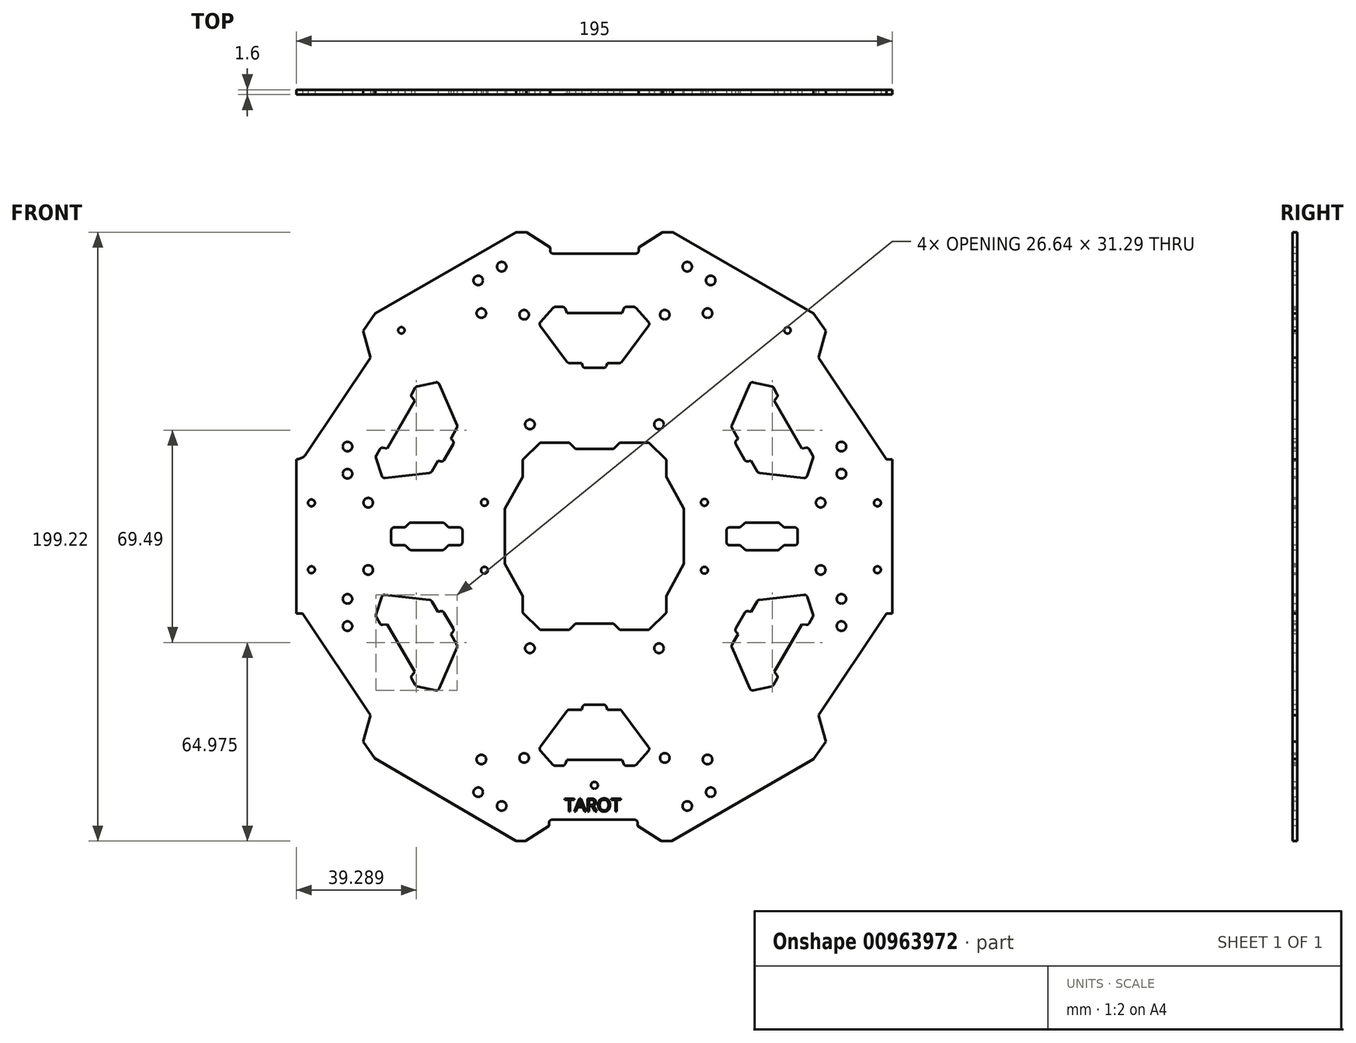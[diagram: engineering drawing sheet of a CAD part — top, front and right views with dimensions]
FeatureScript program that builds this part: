
annotation { "Feature Type Name" : "Feature", "Feature Type Description" : "" }
export const myFeature = defineFeature(function(context is Context, id is Id, definition is map)
    precondition{}
    {
        {
            var Q0;
            Q0=qCreatedBy(makeId("Front.planeOp"),FACE);
            var sketch = newSketch(context, id + "F0", { "sketchPlane" : qUnion([Q0])});
            skLineSegment(sketch, "E0.0", {"start": v(-55.43, 99) * mm, "end": v(57.16, 99) * mm});
            skLineSegment(sketch, "E0.1", {"start": v(57.16, 99) * mm, "end": v(113.45, 1.5) * mm});
            skLineSegment(sketch, "E0.2", {"start": v(113.45, 1.5) * mm, "end": v(55.43, -99) * mm});
            skLineSegment(sketch, "E0.3", {"start": v(55.43, -99) * mm, "end": v(-57.6, -99) * mm});
            skLineSegment(sketch, "E0.4", {"start": v(-57.6, -99) * mm, "end": v(-113.24, -1.13) * mm});
            skLineSegment(sketch, "E0.5", {"start": v(-113.24, -1.13) * mm, "end": v(-55.43, 99) * mm});
            skPoint(sketch, "E0.0.midPoint", {"position": v(0.87, 99) * mm});
            skSolve(sketch);
        }
        {
            var Q0;
            Q0 = qSketchRegion(id + "F0", true);
            extrude(context, id + "F1", {"entities" : qUnion([Q0]), "depth" : 1.6 * mm, "offsetDistance" : 25 * mm});
        }
        {
            var Q0;
            Q0=makeQuery(id+"F1.opExtrude","CAP_FACE",FACE,{"disambiguationData":[OSD([sQuery(id+"F0.wireOp",EDGE,"E0.0"),sQuery(id+"F0.wireOp",EDGE,"E0.1"),sQuery(id+"F0.wireOp",EDGE,"E0.2"),sQuery(id+"F0.wireOp",EDGE,"E0.3"),sQuery(id+"F0.wireOp",EDGE,"E0.4"),sQuery(id+"F0.wireOp",EDGE,"E0.5")])],"isStart":false});
            var sketch = newSketch(context, id + "F2", { "sketchPlane" : qUnion([Q0])});
            skLineSegment(sketch, "E1", {"start": v(0, 0) * mm, "end": v(0, 99) * mm, "construction": true});
            skLineSegment(sketch, "E2", {"start": v(-25.62, 99) * mm, "end": v(-25.62, 82.49) * mm, "construction": true});
            skLineSegment(sketch, "E3", {"start": v(25.63, 99) * mm, "end": v(25.63, 87.55) * mm, "construction": true});
            skLineSegment(sketch, "E4", {"start": v(-25.62, 99) * mm, "end": v(0, 99) * mm, "construction": true});
            skLineSegment(sketch, "E5", {"start": v(25.62, 99) * mm, "end": v(0, 99) * mm, "construction": true});
            skLineSegment(sketch, "E6", {"start": v(-25.62, 99) * mm, "end": v(-33.12, 99) * mm, "construction": true});
            skLineSegment(sketch, "E7", {"start": v(0, 0) * mm, "end": v(-84.33, 48.69) * mm, "construction": true});
            skPoint(sketch, "E7.endSnap0", {"position": v(-84.33, 48.93) * mm});
            skLineSegment(sketch, "E8", {"start": v(-96.83, 27.28) * mm, "end": v(-84.63, 20.24) * mm, "construction": true});
            skLineSegment(sketch, "E9", {"start": v(-71.83, 70.58) * mm, "end": v(-70.08, 69.58) * mm, "construction": true});
            skLineSegment(sketch, "E10", {"start": v(-96.83, 27.28) * mm, "end": v(-84.33, 48.93) * mm, "construction": true});
            skLineSegment(sketch, "E11", {"start": v(-71.83, 70.58) * mm, "end": v(-84.33, 48.93) * mm, "construction": true});
            skLineSegment(sketch, "E12", {"start": v(-70.08, 69.58) * mm, "end": v(-71.83, 70.58) * mm});
            skLineSegment(sketch, "E13", {"start": v(-71.83, 70.58) * mm, "end": v(-55.43, 99) * mm});
            skLineSegment(sketch, "E14", {"start": v(-55.43, 99) * mm, "end": v(-33.12, 99) * mm});
            skLineSegment(sketch, "E15", {"start": v(0, 0) * mm, "end": v(24.48, 42.4) * mm, "construction": true});
            skLineSegment(sketch, "E16", {"start": v(-70.08, 69.58) * mm, "end": v(-34.22, 87.3) * mm});
            skLineSegment(sketch, "E17", {"start": v(-25.62, 99) * mm, "end": v(-31.95, 96) * mm});
            skLineSegment(sketch, "E18", {"start": v(-31.95, 96) * mm, "end": v(-34.22, 87.3) * mm});
            skLineSegment(sketch, "E19.MirrorCS", {"start": v(-95.3, 25.9) * mm, "end": v(-97.04, 26.92) * mm});
            skLineSegment(sketch, "E20.MirrorCS", {"start": v(-97.04, 26.92) * mm, "end": v(-95.3, 25.9) * mm, "construction": true});
            skLineSegment(sketch, "E21.MirrorCS", {"start": v(-99.11, -20.33) * mm, "end": v(-92.7, -14) * mm});
            skLineSegment(sketch, "E22.MirrorCS", {"start": v(-98.55, -27.3) * mm, "end": v(-102.3, -20.81) * mm, "construction": true});
            skLineSegment(sketch, "E23.MirrorCS", {"start": v(-98.55, -27.3) * mm, "end": v(-99.11, -20.33) * mm});
            skPoint(sketch, "E24.MirrorP", {"position": v(-84.54, 48.57) * mm});
            skLineSegment(sketch, "E25.MirrorCS", {"start": v(-98.55, -27.3) * mm, "end": v(-84.25, -19.05) * mm, "construction": true});
            skLineSegment(sketch, "E26.MirrorCS", {"start": v(-97.04, 26.92) * mm, "end": v(-113.45, -1.5) * mm});
            skLineSegment(sketch, "E27.MirrorCS", {"start": v(-95.3, 25.9) * mm, "end": v(-92.7, -14) * mm});
            skLineSegment(sketch, "E28.MirrorCS", {"start": v(-113.45, -1.5) * mm, "end": v(-102.3, -20.81) * mm});
            skLineSegment(sketch, "E29.MirrorCS", {"start": v(70.08, -69.58) * mm, "end": v(71.83, -70.58) * mm});
            skLineSegment(sketch, "E30.MirrorCS", {"start": v(71.83, -70.58) * mm, "end": v(70.08, -69.58) * mm, "construction": true});
            skLineSegment(sketch, "E31.MirrorCS", {"start": v(95.3, -25.9) * mm, "end": v(97.04, -26.92) * mm});
            skLineSegment(sketch, "E32.MirrorCS", {"start": v(97.04, -26.92) * mm, "end": v(95.3, -25.9) * mm, "construction": true});
            skLineSegment(sketch, "E33.MirrorCS", {"start": v(31.95, -96) * mm, "end": v(34.22, -87.3) * mm});
            skLineSegment(sketch, "E34.MirrorCS", {"start": v(98.55, 27.3) * mm, "end": v(99.11, 20.33) * mm});
            skLineSegment(sketch, "E35.MirrorCS", {"start": v(98.55, 27.3) * mm, "end": v(102.3, 20.81) * mm, "construction": true});
            skLineSegment(sketch, "E36.MirrorCS", {"start": v(25.63, -99) * mm, "end": v(33.13, -99) * mm, "construction": true});
            skLineSegment(sketch, "E37.MirrorCS", {"start": v(25.62, -99) * mm, "end": v(31.95, -96) * mm});
            skLineSegment(sketch, "E38.MirrorCS", {"start": v(99.11, 20.33) * mm, "end": v(92.7, 14) * mm});
            skPoint(sketch, "E39.MirrorP", {"position": v(84.33, -48.93) * mm});
            skLineSegment(sketch, "E40.MirrorCS", {"start": v(72.04, -70.22) * mm, "end": v(59.84, -63.17) * mm, "construction": true});
            skLineSegment(sketch, "E41.MirrorCS", {"start": v(95.3, -25.9) * mm, "end": v(92.7, 14) * mm});
            skLineSegment(sketch, "E42.MirrorCS", {"start": v(25.63, -99) * mm, "end": v(25.63, -82.49) * mm, "construction": true});
            skLineSegment(sketch, "E43.MirrorCS", {"start": v(72.04, -70.22) * mm, "end": v(84.54, -48.57) * mm, "construction": true});
            skLineSegment(sketch, "E44.MirrorCS", {"start": v(113.45, 1.5) * mm, "end": v(102.3, 20.81) * mm});
            skLineSegment(sketch, "E45.MirrorCS", {"start": v(97.04, -26.92) * mm, "end": v(113.45, 1.5) * mm});
            skLineSegment(sketch, "E46.MirrorCS", {"start": v(97.04, -26.92) * mm, "end": v(84.54, -48.57) * mm, "construction": true});
            skLineSegment(sketch, "E47.MirrorCS", {"start": v(70.08, -69.58) * mm, "end": v(34.22, -87.3) * mm});
            skPoint(sketch, "E48.MirrorP", {"position": v(84.54, -48.57) * mm});
            skLineSegment(sketch, "E49.MirrorCS", {"start": v(71.83, -70.58) * mm, "end": v(55.43, -99) * mm});
            skLineSegment(sketch, "E50.MirrorCS", {"start": v(55.43, -99) * mm, "end": v(33.12, -99) * mm});
            skLineSegment(sketch, "E51.MirrorCS", {"start": v(98.55, 27.3) * mm, "end": v(84.25, 19.05) * mm, "construction": true});
            skSolve(sketch);
        }
        {
            var Q0;
            Q0=makeQuery(id+"F2.imprint","IMPRINT",FACE,{"disambiguationData":[TD([[makeQuery(id+"F2.imprint","IMPRINT",EDGE,{"derivedFrom":sQuery(id+"F2.wireOp",EDGE,"E12")}),-1.0]])]});
            var Q1;
            {var subQ3=sQuery(id+"F2.wireOp",EDGE,"E19.MirrorCS");Q1=makeQuery(id+"F2.imprint","IMPRINT",FACE,{"disambiguationData":[TD([[makeQuery(id+"F2.imprint","IMPRINT",EDGE,{"derivedFrom":subQ3}),1.0]])]});}
            var Q2;
            Q2=makeQuery(id+"F2.imprint","IMPRINT",FACE,{"disambiguationData":[TD([[makeQuery(id+"F2.imprint","IMPRINT",EDGE,{"derivedFrom":sQuery(id+"F2.wireOp",EDGE,"E29.MirrorCS")}),-1.0]])]});
            var Q3;
            Q3=makeQuery(id+"F2.imprint","IMPRINT",FACE,{"disambiguationData":[TD([[makeQuery(id+"F2.imprint","IMPRINT",EDGE,{"derivedFrom":sQuery(id+"F2.wireOp",EDGE,"E31.MirrorCS")}),1.0]])]});
            extrude(context, id + "F3", {"entities" : qUnion([Q0, Q1, Q2, Q3]), "operationType" : NewBodyOperationType.REMOVE, "oppositeDirection" : true, "depth" : 25 * mm, "offsetDistance" : 25 * mm});
        }
        {
            var Q0;
            Q0=qCreatedBy(makeId("Right.planeOp"),FACE);
            var sketch = newSketch(context, id + "F4", { "sketchPlane" : qUnion([Q0])});
            skLineSegment(sketch, "E52", {"start": v(0, 0) * mm, "end": v(-52.74, 0) * mm});
            skSolve(sketch);
        }
        {
            var Q0;
            Q0=makeQuery(id+"F1.opExtrude","SWEPT_BODY",BODY,{"disambiguationData":[OSD([sQuery(id+"F0.wireOp",EDGE,"E0.0"),sQuery(id+"F0.wireOp",EDGE,"E0.1"),sQuery(id+"F0.wireOp",EDGE,"E0.2"),sQuery(id+"F0.wireOp",EDGE,"E0.3"),sQuery(id+"F0.wireOp",EDGE,"E0.4"),sQuery(id+"F0.wireOp",EDGE,"E0.5")])]});
            var Q1;
            Q1=sQuery(id+"F4.wireOp",EDGE,"E52");
            transform(context, id + "F5", {"entities" : qUnion([Q0]), "transformType" : TransformType.ROTATION, "transformAxis" : qUnion([Q1]), "angle" : 30 * degree, "makeCopy" : false});
        }
        {
            var Q0;
            Q0=makeQuery(id+"F1.opExtrude","CAP_FACE",FACE,{"disambiguationData":[OSD([sQuery(id+"F0.wireOp",EDGE,"E0.0"),sQuery(id+"F0.wireOp",EDGE,"E0.1"),sQuery(id+"F0.wireOp",EDGE,"E0.2"),sQuery(id+"F0.wireOp",EDGE,"E0.3"),sQuery(id+"F0.wireOp",EDGE,"E0.4"),sQuery(id+"F0.wireOp",EDGE,"E0.5")])],"isStart":false});
            var sketch = newSketch(context, id + "F6", { "sketchPlane" : qUnion([Q0])});
            skLineSegment(sketch, "E53", {"start": v(0, 0) * mm, "end": v(0, 92.5) * mm, "construction": true});
            skLineSegment(sketch, "E54", {"start": v(0, 92.5) * mm, "end": v(-14.5, 92.5) * mm});
            skLineSegment(sketch, "E55", {"start": v(0, 92.5) * mm, "end": v(14.5, 92.5) * mm});
            skLineSegment(sketch, "E56", {"start": v(-14.5, 92.5) * mm, "end": v(-14.5, 94.5) * mm});
            skLineSegment(sketch, "E57", {"start": v(-14.5, 94.5) * mm, "end": v(-14.5, 99.5) * mm, "construction": true});
            skLineSegment(sketch, "E58", {"start": v(-14.5, 99.5) * mm, "end": v(-22.25, 99.5) * mm, "construction": true});
            skLineSegment(sketch, "E59", {"start": v(-14.5, 94.5) * mm, "end": v(-22.25, 99.5) * mm});
            skLineSegment(sketch, "E60", {"start": v(-22.25, 99.5) * mm, "end": v(-25.66, 99.5) * mm});
            skLineSegment(sketch, "E61.MirrorCS", {"start": v(14.5, 99.5) * mm, "end": v(22.25, 99.5) * mm, "construction": true});
            skLineSegment(sketch, "E62.MirrorCS", {"start": v(14.5, 94.5) * mm, "end": v(14.5, 99.5) * mm, "construction": true});
            skLineSegment(sketch, "E63.MirrorCS", {"start": v(22.25, 99.5) * mm, "end": v(25.66, 99.5) * mm});
            skLineSegment(sketch, "E64.MirrorCS", {"start": v(14.5, 94.5) * mm, "end": v(22.25, 99.5) * mm});
            skLineSegment(sketch, "E65", {"start": v(14.5, 92.5) * mm, "end": v(14.5, 94.5) * mm});
            skLineSegment(sketch, "E66", {"start": v(-25.66, 99.5) * mm, "end": v(0, 114.32) * mm});
            skLineSegment(sketch, "E67", {"start": v(0, 114.32) * mm, "end": v(25.66, 99.5) * mm});
            skLineSegment(sketch, "E68", {"start": v(-0.38, -92.72) * mm, "end": v(14.12, -92.72) * mm});
            skLineSegment(sketch, "E69", {"start": v(-0.38, -92.72) * mm, "end": v(-14.88, -92.72) * mm});
            skLineSegment(sketch, "E70", {"start": v(14.12, -92.72) * mm, "end": v(14.12, -94.72) * mm});
            skLineSegment(sketch, "E71", {"start": v(14.12, -94.72) * mm, "end": v(14.12, -99.72) * mm, "construction": true});
            skLineSegment(sketch, "E72", {"start": v(14.12, -99.72) * mm, "end": v(21.87, -99.72) * mm, "construction": true});
            skLineSegment(sketch, "E73", {"start": v(14.12, -94.72) * mm, "end": v(21.87, -99.72) * mm});
            skLineSegment(sketch, "E74", {"start": v(21.87, -99.72) * mm, "end": v(25.28, -99.72) * mm});
            skLineSegment(sketch, "E75.MirrorCS", {"start": v(-14.88, -99.72) * mm, "end": v(-22.63, -99.72) * mm, "construction": true});
            skLineSegment(sketch, "E76.MirrorCS", {"start": v(-14.88, -94.72) * mm, "end": v(-14.88, -99.72) * mm, "construction": true});
            skLineSegment(sketch, "E77.MirrorCS", {"start": v(-22.63, -99.72) * mm, "end": v(-26.04, -99.72) * mm});
            skLineSegment(sketch, "E78.MirrorCS", {"start": v(-14.88, -94.72) * mm, "end": v(-22.63, -99.72) * mm});
            skLineSegment(sketch, "E79", {"start": v(-14.88, -92.72) * mm, "end": v(-14.88, -94.72) * mm});
            skLineSegment(sketch, "E80", {"start": v(25.28, -99.72) * mm, "end": v(-0.38, -114.53) * mm});
            skLineSegment(sketch, "E81", {"start": v(-0.38, -114.53) * mm, "end": v(-26.04, -99.72) * mm});
            skSolve(sketch);
        }
        {
            var Q0;
            Q0 = qSketchRegion(id + "F6", true);
            extrude(context, id + "F7", {"entities" : qUnion([Q0]), "operationType" : NewBodyOperationType.REMOVE, "oppositeDirection" : true, "depth" : 25 * mm, "offsetDistance" : 25 * mm});
        }
        {
            var Q0;
            Q0=makeQuery(id+"F1.opExtrude","CAP_FACE",FACE,{"disambiguationData":[OSD([sQuery(id+"F0.wireOp",EDGE,"E0.0"),sQuery(id+"F0.wireOp",EDGE,"E0.1"),sQuery(id+"F0.wireOp",EDGE,"E0.2"),sQuery(id+"F0.wireOp",EDGE,"E0.3"),sQuery(id+"F0.wireOp",EDGE,"E0.4"),sQuery(id+"F0.wireOp",EDGE,"E0.5")])],"isStart":false});
            var sketch = newSketch(context, id + "F8", { "sketchPlane" : qUnion([Q0])});
            skLineSegment(sketch, "E82.bottom", {"start": v(21.13, 36.62) * mm, "end": v(-21.13, 36.62) * mm, "construction": true});
            skLineSegment(sketch, "E82.top", {"start": v(21.12, -36.62) * mm, "end": v(-21.13, -36.62) * mm, "construction": true});
            skLineSegment(sketch, "E82.left", {"start": v(21.13, 36.62) * mm, "end": v(21.12, -36.62) * mm, "construction": true});
            skLineSegment(sketch, "E82.right", {"start": v(-21.13, 36.62) * mm, "end": v(-21.13, -36.62) * mm, "construction": true});
            skPoint(sketch, "E82.middle", {"position": v(0, 0) * mm});
            skCircle(sketch, "E83", {"center": v(-21.13, 36.62) * mm, "radius": 1.57 * mm});
            skCircle(sketch, "E84", {"center": v(21.13, 36.62) * mm, "radius": 1.57 * mm});
            skCircle(sketch, "E85", {"center": v(-21.13, -36.62) * mm, "radius": 1.57 * mm});
            skCircle(sketch, "E86", {"center": v(21.12, -36.62) * mm, "radius": 1.57 * mm});
            skLineSegment(sketch, "E87.bottom", {"start": v(-35.98, 11.1) * mm, "end": v(35.98, 11.1) * mm, "construction": true});
            skLineSegment(sketch, "E87.top", {"start": v(-35.98, -11.1) * mm, "end": v(35.98, -11.1) * mm, "construction": true});
            skLineSegment(sketch, "E87.left", {"start": v(-35.98, 11.1) * mm, "end": v(-35.98, -11.1) * mm, "construction": true});
            skLineSegment(sketch, "E87.right", {"start": v(35.98, 11.1) * mm, "end": v(35.98, -11.1) * mm, "construction": true});
            skCircle(sketch, "E88", {"center": v(-35.98, 11.1) * mm, "radius": 1.13 * mm});
            skCircle(sketch, "E89", {"center": v(-35.98, -11.1) * mm, "radius": 1.13 * mm});
            skCircle(sketch, "E90", {"center": v(35.98, 11.1) * mm, "radius": 1.12 * mm});
            skCircle(sketch, "E91", {"center": v(35.98, -11.1) * mm, "radius": 1.13 * mm});
            skLineSegment(sketch, "E92", {"start": v(-23, 72.5) * mm, "end": v(23, 72.5) * mm, "construction": true});
            skLineSegment(sketch, "E93", {"start": v(0, 72.5) * mm, "end": v(0, 59.38) * mm, "construction": true});
            skCircle(sketch, "E94", {"center": v(-23, 72.5) * mm, "radius": 1.55 * mm});
            skCircle(sketch, "E95", {"center": v(23, 72.5) * mm, "radius": 1.55 * mm});
            skCircle(sketch, "E96.MirrorC", {"center": v(23, -72.5) * mm, "radius": 1.55 * mm});
            skCircle(sketch, "E97.MirrorC", {"center": v(-23, -72.5) * mm, "radius": 1.55 * mm});
            skLineSegment(sketch, "E98.MirrorCS", {"start": v(-23, -72.5) * mm, "end": v(23, -72.5) * mm, "construction": true});
            skLineSegment(sketch, "E99", {"start": v(-37, 73) * mm, "end": v(37, 73) * mm, "construction": true});
            skLineSegment(sketch, "E100", {"start": v(0, 80.25) * mm, "end": v(0, 73) * mm, "construction": true});
            skCircle(sketch, "E101", {"center": v(-37, 73) * mm, "radius": 1.55 * mm});
            skCircle(sketch, "E102", {"center": v(37, 73) * mm, "radius": 1.55 * mm});
            skCircle(sketch, "E103.MirrorC", {"center": v(-37, -73) * mm, "radius": 1.55 * mm});
            skCircle(sketch, "E104.MirrorC", {"center": v(37, -73) * mm, "radius": 1.55 * mm});
            skCircle(sketch, "E105", {"center": v(0, -81.47) * mm, "radius": 1.13 * mm});
            skCircle(sketch, "E106", {"center": v(-63.15, 67.4) * mm, "radius": 1.05 * mm});
            skLineSegment(sketch, "E107", {"start": v(-63.15, 67.4) * mm, "end": v(63.15, 67.4) * mm, "construction": true});
            skLineSegment(sketch, "E108", {"start": v(0, 67.4) * mm, "end": v(0, 57.3) * mm, "construction": true});
            skCircle(sketch, "E109", {"center": v(63.15, 67.4) * mm, "radius": 1.05 * mm});
            skSolve(sketch);
        }
        {
            var Q0;
            Q0=makeQuery(id+"F7.boolean.opBoolean","COPY",EDGE,{"derivedFrom":makeQuery(id+"F7.opExtrude","SWEPT_EDGE",EDGE,{"disambiguationData":[OSD([sQuery(id+"F6.wireOp",EDGE,"E54"),sQuery(id+"F6.wireOp",EDGE,"E56")])]})});
            var Q1;
            Q1=makeQuery(id+"F7.boolean.opBoolean","COPY",EDGE,{"derivedFrom":makeQuery(id+"F7.opExtrude","SWEPT_EDGE",EDGE,{"disambiguationData":[OSD([sQuery(id+"F6.wireOp",EDGE,"E55"),sQuery(id+"F6.wireOp",EDGE,"E65")])]})});
            var Q2;
            Q2=makeQuery(id+"F3.boolean.opBoolean","COPY",EDGE,{"derivedFrom":makeQuery(id+"F3.opExtrude","SWEPT_EDGE",EDGE,{"disambiguationData":[OSD([sQuery(id+"F2.wireOp",EDGE,"3c353f30-4fd9-4b19-be87-6d07171912626.MirrorCS"),sQuery(id+"F2.wireOp",EDGE,"3c353f30-4fd9-4b19-be87-6d07171912627.MirrorCS")])]})});
            var Q3;
            Q3=makeQuery(id+"F3.boolean.opBoolean","COPY",EDGE,{"derivedFrom":makeQuery(id+"F3.opExtrude","SWEPT_EDGE",EDGE,{"disambiguationData":[OSD([sQuery(id+"F2.wireOp",EDGE,"ab6a4181-ef32-43c6-bda4-39222323dd7e2.MirrorCS"),sQuery(id+"F2.wireOp",EDGE,"ab6a4181-ef32-43c6-bda4-39222323dd7e4.MirrorCS")])]})});
            var Q4;
            Q4=makeQuery(id+"F3.boolean.opBoolean","COPY",EDGE,{"derivedFrom":makeQuery(id+"F3.opExtrude","SWEPT_EDGE",EDGE,{"disambiguationData":[OSD([sQuery(id+"F2.wireOp",EDGE,"yAr7u7Sg-ti8k-CcrC-Hcsy-DfrhCiWDHcSb"),sQuery(id+"F2.wireOp",EDGE,"wbw0Cuhm-vE27-KPKq-b3XP-NUPUyRbLNj7i")])]})});
            var Q5;
            Q5=makeQuery(id+"F3.boolean.opBoolean","COPY",EDGE,{"derivedFrom":makeQuery(id+"F3.opExtrude","SWEPT_EDGE",EDGE,{"disambiguationData":[OSD([sQuery(id+"F2.wireOp",EDGE,"5a6e3571-f0e1-4f9f-8eac-d765dfb8e4a70.MirrorCS"),sQuery(id+"F2.wireOp",EDGE,"a7f60a59-f831-41f1-b416-a16ffb49d1590.MirrorCS")])]})});
            var Q6;
            Q6=makeQuery(id+"F7.boolean.opBoolean","COPY",EDGE,{"derivedFrom":makeQuery(id+"F7.opExtrude","SWEPT_EDGE",EDGE,{"disambiguationData":[OSD([sQuery(id+"F6.wireOp",EDGE,"E69"),sQuery(id+"F6.wireOp",EDGE,"E79")])]})});
            var Q7;
            Q7=makeQuery(id+"F7.boolean.opBoolean","COPY",EDGE,{"derivedFrom":makeQuery(id+"F7.opExtrude","SWEPT_EDGE",EDGE,{"disambiguationData":[OSD([sQuery(id+"F6.wireOp",EDGE,"E68"),sQuery(id+"F6.wireOp",EDGE,"E70")])]})});
            fillet(context, id + "F9", {"entities" : qUnion([Q0, Q1, Q2, Q3, Q4, Q5, Q6, Q7]), "radius" : 1 * mm, "tangentPropagation" : true, "allowEdgeOverflow" : false});
        }
        {
            var Q0;
            Q0=makeQuery(id+"F3.boolean.opBoolean","COPY",EDGE,{"derivedFrom":makeQuery(id+"F3.opExtrude","SWEPT_EDGE",EDGE,{"disambiguationData":[OSD([sQuery(id+"F2.wireOp",EDGE,"3c353f30-4fd9-4b19-be87-6d07171912620.MirrorCS"),sQuery(id+"F2.wireOp",EDGE,"3c353f30-4fd9-4b19-be87-6d07171912627.MirrorCS")])]})});
            var Q1;
            Q1=makeQuery(id+"F3.boolean.opBoolean","COPY",EDGE,{"derivedFrom":makeQuery(id+"F3.opExtrude","SWEPT_EDGE",EDGE,{"disambiguationData":[OSD([sQuery(id+"F2.wireOp",EDGE,"ab6a4181-ef32-43c6-bda4-39222323dd7e0.MirrorCS"),sQuery(id+"F2.wireOp",EDGE,"ab6a4181-ef32-43c6-bda4-39222323dd7e4.MirrorCS")])]})});
            var Q2;
            Q2=makeQuery(id+"F3.boolean.opBoolean","COPY",EDGE,{"derivedFrom":makeQuery(id+"F3.opExtrude","SWEPT_EDGE",EDGE,{"disambiguationData":[OSD([sQuery(id+"F2.wireOp",EDGE,"5a6e3571-f0e1-4f9f-8eac-d765dfb8e4a70.MirrorCS"),sQuery(id+"F2.wireOp",EDGE,"EQJ7UQQr-2yyt-cUzk-Uep8-xCyMp42e8Ayk")])]})});
            var Q3;
            Q3=makeQuery(id+"F3.boolean.opBoolean","COPY",EDGE,{"derivedFrom":makeQuery(id+"F3.opExtrude","SWEPT_EDGE",EDGE,{"disambiguationData":[OSD([sQuery(id+"F2.wireOp",EDGE,"wbw0Cuhm-vE27-KPKq-b3XP-NUPUyRbLNj7i"),sQuery(id+"F2.wireOp",EDGE,"E12")])]})});
            fillet(context, id + "F10", {"entities" : qUnion([Q0, Q1, Q2, Q3]), "radius" : 4 * mm, "tangentPropagation" : true, "allowEdgeOverflow" : false});
        }
        {
            var Q0;
            Q0 = qSketchRegion(id + "F8", true);
            extrude(context, id + "F11", {"entities" : qUnion([Q0]), "operationType" : NewBodyOperationType.REMOVE, "oppositeDirection" : true, "depth" : 25 * mm, "offsetDistance" : 25 * mm});
        }
        {
            var Q0;
            Q0=makeQuery(id+"F1.opExtrude","CAP_FACE",FACE,{"disambiguationData":[OSD([sQuery(id+"F0.wireOp",EDGE,"E0.0"),sQuery(id+"F0.wireOp",EDGE,"E0.1"),sQuery(id+"F0.wireOp",EDGE,"E0.2"),sQuery(id+"F0.wireOp",EDGE,"E0.3"),sQuery(id+"F0.wireOp",EDGE,"E0.4"),sQuery(id+"F0.wireOp",EDGE,"E0.5")])],"isStart":false});
            var sketch = newSketch(context, id + "F12", { "sketchPlane" : qUnion([Q0])});
            skCircle(sketch, "E110", {"center": v(-92.57, -10.93) * mm, "radius": 1.13 * mm});
            skLineSegment(sketch, "E111", {"start": v(-92.57, -10.93) * mm, "end": v(-92.57, 10.93) * mm, "construction": true});
            skLineSegment(sketch, "E112", {"start": v(-92.57, 0) * mm, "end": v(0, 0) * mm, "construction": true});
            skCircle(sketch, "E113", {"center": v(-92.57, 10.93) * mm, "radius": 1.13 * mm});
            skLineSegment(sketch, "E114", {"start": v(0, 0) * mm, "end": v(0, 28.32) * mm, "construction": true});
            skCircle(sketch, "E115.MirrorC", {"center": v(92.58, -10.93) * mm, "radius": 1.13 * mm});
            skCircle(sketch, "E116.MirrorC", {"center": v(92.58, 10.93) * mm, "radius": 1.13 * mm});
            skLineSegment(sketch, "E117.MirrorCS", {"start": v(92.58, -10.93) * mm, "end": v(92.58, 10.93) * mm, "construction": true});
            skLineSegment(sketch, "E118.bottom", {"start": v(-74, 11) * mm, "end": v(74, 11) * mm, "construction": true});
            skLineSegment(sketch, "E118.top", {"start": v(-74, -11) * mm, "end": v(74, -11) * mm, "construction": true});
            skLineSegment(sketch, "E118.left", {"start": v(-74, 11) * mm, "end": v(-74, -11) * mm, "construction": true});
            skLineSegment(sketch, "E118.right", {"start": v(74, 11) * mm, "end": v(74, -11) * mm, "construction": true});
            skPoint(sketch, "E118.middle", {"position": v(0, 0) * mm});
            skCircle(sketch, "E119", {"center": v(-74, 11) * mm, "radius": 1.55 * mm});
            skCircle(sketch, "E120", {"center": v(-74, -11) * mm, "radius": 1.55 * mm});
            skCircle(sketch, "E121", {"center": v(74, 11) * mm, "radius": 1.55 * mm});
            skCircle(sketch, "E122", {"center": v(74, -11) * mm, "radius": 1.55 * mm});
            skLineSegment(sketch, "E123", {"start": v(-92.57, -10.92) * mm, "end": v(-80.78, -20.47) * mm, "construction": true});
            skLineSegment(sketch, "E124", {"start": v(-80.78, -20.47) * mm, "end": v(-74, -11) * mm, "construction": true});
            skCircle(sketch, "E125", {"center": v(-80.78, -20.47) * mm, "radius": 1.55 * mm});
            skLineSegment(sketch, "E126", {"start": v(-80.78, -20.47) * mm, "end": v(-80.78, -29.37) * mm, "construction": true});
            skCircle(sketch, "E127", {"center": v(-80.78, -29.37) * mm, "radius": 1.55 * mm});
            skLineSegment(sketch, "E128.MirrorCS", {"start": v(-92.57, 10.92) * mm, "end": v(-80.78, 20.47) * mm, "construction": true});
            skLineSegment(sketch, "E129.MirrorCS", {"start": v(-80.78, 20.47) * mm, "end": v(-74, 11) * mm, "construction": true});
            skCircle(sketch, "E130.MirrorC", {"center": v(-80.78, 20.47) * mm, "radius": 1.55 * mm});
            skCircle(sketch, "E131.MirrorC", {"center": v(-80.78, 29.37) * mm, "radius": 1.55 * mm});
            skLineSegment(sketch, "E132.MirrorCS", {"start": v(-80.78, 20.47) * mm, "end": v(-80.78, 29.37) * mm, "construction": true});
            skCircle(sketch, "E133.MirrorC", {"center": v(80.78, -20.47) * mm, "radius": 1.55 * mm});
            skLineSegment(sketch, "E134.MirrorCS", {"start": v(80.78, -20.47) * mm, "end": v(80.78, -29.37) * mm, "construction": true});
            skCircle(sketch, "E135.MirrorC", {"center": v(80.78, -29.37) * mm, "radius": 1.55 * mm});
            skLineSegment(sketch, "E136.MirrorCS", {"start": v(80.78, 20.47) * mm, "end": v(80.78, 29.37) * mm, "construction": true});
            skCircle(sketch, "E137.MirrorC", {"center": v(80.78, 29.37) * mm, "radius": 1.55 * mm});
            skCircle(sketch, "E138.MirrorC", {"center": v(80.78, 20.47) * mm, "radius": 1.55 * mm});
            skCircle(sketch, "E139", {"center": v(-30.35, -88.21) * mm, "radius": 1.55 * mm});
            skLineSegment(sketch, "E140", {"start": v(-30.35, -88.21) * mm, "end": v(-38.03, -83.71) * mm, "construction": true});
            skCircle(sketch, "E141", {"center": v(-38.03, -83.71) * mm, "radius": 1.55 * mm});
            skLineSegment(sketch, "E142", {"start": v(-30.35, -88.21) * mm, "end": v(30.35, -88.21) * mm, "construction": true});
            skLineSegment(sketch, "E143", {"start": v(0, -88.21) * mm, "end": v(0, -43.95) * mm, "construction": true});
            skCircle(sketch, "E144.MirrorC", {"center": v(38.03, -83.71) * mm, "radius": 1.55 * mm});
            skCircle(sketch, "E145.MirrorC", {"center": v(30.35, -88.21) * mm, "radius": 1.55 * mm});
            skLineSegment(sketch, "E146.MirrorCS", {"start": v(30.35, -88.21) * mm, "end": v(38.03, -83.71) * mm, "construction": true});
            skCircle(sketch, "E147.MirrorC", {"center": v(-30.35, 88.21) * mm, "radius": 1.55 * mm});
            skLineSegment(sketch, "E148.MirrorCS", {"start": v(-30.35, 88.21) * mm, "end": v(-38.03, 83.71) * mm, "construction": true});
            skCircle(sketch, "E149.MirrorC", {"center": v(30.35, 88.21) * mm, "radius": 1.55 * mm});
            skCircle(sketch, "E150.MirrorC", {"center": v(-38.03, 83.71) * mm, "radius": 1.55 * mm});
            skCircle(sketch, "E151.MirrorC", {"center": v(38.03, 83.71) * mm, "radius": 1.55 * mm});
            skLineSegment(sketch, "E152.MirrorCS", {"start": v(30.35, 88.21) * mm, "end": v(38.03, 83.71) * mm, "construction": true});
            skLineSegment(sketch, "E153.MirrorCS", {"start": v(0, 88.21) * mm, "end": v(0, 43.95) * mm, "construction": true});
            skLineSegment(sketch, "E154.MirrorCS", {"start": v(-30.35, 88.21) * mm, "end": v(30.35, 88.21) * mm, "construction": true});
            skSolve(sketch);
        }
        {
            var Q0;
            Q0 = qSketchRegion(id + "F12", true);
            extrude(context, id + "F13", {"entities" : qUnion([Q0]), "operationType" : NewBodyOperationType.REMOVE, "oppositeDirection" : true, "depth" : 25 * mm, "offsetDistance" : 25 * mm});
        }
        {
            var Q0;
            Q0=makeQuery(id+"F1.opExtrude","CAP_FACE",FACE,{"disambiguationData":[OSD([sQuery(id+"F0.wireOp",EDGE,"E0.0"),sQuery(id+"F0.wireOp",EDGE,"E0.1"),sQuery(id+"F0.wireOp",EDGE,"E0.2"),sQuery(id+"F0.wireOp",EDGE,"E0.3"),sQuery(id+"F0.wireOp",EDGE,"E0.4"),sQuery(id+"F0.wireOp",EDGE,"E0.5")])],"isStart":false});
            var sketch = newSketch(context, id + "F14", { "sketchPlane" : qUnion([Q0])});
            skText(sketch, "E155", { "text": "TAROT", "fontName": "OpenSans-Regular.ttf"});
            const initialGuessF14  = {"E155": [-0.0098, -0.09001, 1, 0, 0.00425]};
            skSetInitialGuess(sketch, initialGuessF14);
            skSolve(sketch);
        }
        {
            var Q0;
            Q0 = qSketchRegion(id + "F14", true);
            extrude(context, id + "F15", {"entities" : qUnion([Q0]), "operationType" : NewBodyOperationType.REMOVE, "oppositeDirection" : true, "depth" : .3 * mm, "offsetDistance" : 25 * mm});
        }
        {
            var Q0;
            {var subQ0=sQuery(id+"F0.wireOp",EDGE,"E0.5");var subQ1=sQuery(id+"F0.wireOp",EDGE,"E0.4");var subQ2=sQuery(id+"F0.wireOp",EDGE,"E0.3");var subQ3=sQuery(id+"F0.wireOp",EDGE,"E0.2");var subQ4=sQuery(id+"F0.wireOp",EDGE,"E0.1");var subQ5=sQuery(id+"F0.wireOp",EDGE,"E0.0");Q0=makeQuery(id+"F15.boolean.opBoolean","SPLIT",FACE,{"disambiguationData":[TD([makeQuery(id+"F1.opExtrude","SWEPT_FACE",FACE,{"disambiguationData":[OSD([subQ5])]})])],"derivedFrom":makeQuery(id+"F1.opExtrude","CAP_FACE",FACE,{"disambiguationData":[OSD([subQ5,subQ4,subQ3,subQ2,subQ1,subQ0])],"isStart":false})});}
            var sketch = newSketch(context, id + "F16", { "sketchPlane" : qUnion([Q0])});
            skLineSegment(sketch, "E156.left", {"start": v(-29.25, 9) * mm, "end": v(-29.25, 0) * mm});
            skPoint(sketch, "E156.middle", {"position": v(0, 0) * mm});
            skLineSegment(sketch, "E157.bottom", {"start": v(-6.25, 28.6) * mm, "end": v(0, 28.6) * mm});
            skLineSegment(sketch, "E158", {"start": v(-29.25, 9) * mm, "end": v(-23.46, 19.5) * mm});
            skLineSegment(sketch, "E159", {"start": v(-23.46, 19.5) * mm, "end": v(-23.46, 25) * mm});
            skLineSegment(sketch, "E160", {"start": v(-23.46, 25) * mm, "end": v(-17.75, 30.6) * mm});
            skLineSegment(sketch, "E161", {"start": v(-17.75, 30.6) * mm, "end": v(-8.25, 30.6) * mm});
            skLineSegment(sketch, "E162", {"start": v(-8.25, 30.6) * mm, "end": v(-6.25, 28.6) * mm});
            skLineSegment(sketch, "E163", {"start": v(-29.25, 0) * mm, "end": v(0, 0) * mm, "construction": true});
            skLineSegment(sketch, "E164", {"start": v(0, 28.6) * mm, "end": v(0, 0) * mm, "construction": true});
            skPoint(sketch, "E165.orphan", {"position": v(6.25, 28.6) * mm});
            skPoint(sketch, "E166.orphan", {"position": v(-29.25, -9) * mm});
            skLineSegment(sketch, "E167.MirrorCS", {"start": v(8.25, 30.6) * mm, "end": v(6.25, 28.6) * mm});
            skLineSegment(sketch, "E168.MirrorCS", {"start": v(23.46, 19.5) * mm, "end": v(23.46, 25) * mm});
            skLineSegment(sketch, "E169.MirrorCS", {"start": v(23.46, 25) * mm, "end": v(17.75, 30.6) * mm});
            skLineSegment(sketch, "E170.MirrorCS", {"start": v(29.25, 9) * mm, "end": v(29.25, 0) * mm});
            skLineSegment(sketch, "E171.MirrorCS", {"start": v(17.75, 30.6) * mm, "end": v(8.25, 30.6) * mm});
            skLineSegment(sketch, "E172.MirrorCS", {"start": v(29.25, 9) * mm, "end": v(23.46, 19.5) * mm});
            skLineSegment(sketch, "E173", {"start": v(0, 28.6) * mm, "end": v(6.25, 28.6) * mm});
            skLineSegment(sketch, "E174.MirrorCS", {"start": v(-8.25, -30.6) * mm, "end": v(-6.25, -28.6) * mm});
            skLineSegment(sketch, "E175.MirrorCS", {"start": v(8.25, -30.6) * mm, "end": v(6.25, -28.6) * mm});
            skLineSegment(sketch, "E176.MirrorCS", {"start": v(-29.25, -9) * mm, "end": v(-23.46, -19.5) * mm});
            skLineSegment(sketch, "E177.MirrorCS", {"start": v(-29.25, -9) * mm, "end": v(-29.25, 0) * mm});
            skPoint(sketch, "E178.MirrorP", {"position": v(6.25, -28.6) * mm});
            skLineSegment(sketch, "E179.MirrorCS", {"start": v(23.46, -19.5) * mm, "end": v(23.46, -25) * mm});
            skLineSegment(sketch, "E180.MirrorCS", {"start": v(29.25, -9) * mm, "end": v(23.46, -19.5) * mm});
            skPoint(sketch, "E181.MirrorP", {"position": v(-29.25, 9) * mm});
            skLineSegment(sketch, "E182.MirrorCS", {"start": v(-23.46, -19.5) * mm, "end": v(-23.46, -25) * mm});
            skLineSegment(sketch, "E183.MirrorCS", {"start": v(-6.25, -28.6) * mm, "end": v(0, -28.6) * mm});
            skLineSegment(sketch, "E184.MirrorCS", {"start": v(17.75, -30.6) * mm, "end": v(8.25, -30.6) * mm});
            skLineSegment(sketch, "E185.MirrorCS", {"start": v(-17.75, -30.6) * mm, "end": v(-8.25, -30.6) * mm});
            skLineSegment(sketch, "E186.MirrorCS", {"start": v(29.25, -9) * mm, "end": v(29.25, 0) * mm});
            skLineSegment(sketch, "E187.MirrorCS", {"start": v(23.46, -25) * mm, "end": v(17.75, -30.6) * mm});
            skLineSegment(sketch, "E188.MirrorCS", {"start": v(0, -28.6) * mm, "end": v(6.25, -28.6) * mm});
            skLineSegment(sketch, "E189.MirrorCS", {"start": v(0, -28.6) * mm, "end": v(0, 0) * mm, "construction": true});
            skLineSegment(sketch, "E190.MirrorCS", {"start": v(-23.46, -25) * mm, "end": v(-17.75, -30.6) * mm});
            skLineSegment(sketch, "E191", {"start": v(0, 0) * mm, "end": v(0, 73.1) * mm, "construction": true});
            skLineSegment(sketch, "E192", {"start": v(0, 73.1) * mm, "end": v(9, 73.1) * mm});
            skLineSegment(sketch, "E193", {"start": v(9, 73.1) * mm, "end": v(9.5, 74.4) * mm});
            skLineSegment(sketch, "E194", {"start": v(10.44, 75.05) * mm, "end": v(12.8, 75.05) * mm});
            skLineSegment(sketch, "E195", {"start": v(2.98, 55.1) * mm, "end": v(0, 55.1) * mm});
            skLineSegment(sketch, "E196", {"start": v(3.94, 55.85) * mm, "end": v(4.17, 56.7) * mm});
            skLineSegment(sketch, "E197", {"start": v(4.17, 56.7) * mm, "end": v(8.16, 56.7) * mm});
            skLineSegment(sketch, "E198", {"start": v(13.55, 74.72) * mm, "end": v(17.65, 70.16) * mm});
            skLineSegment(sketch, "E199", {"start": v(17.71, 68.9) * mm, "end": v(8.97, 57.1) * mm});
            skPoint(sketch, "E200.visualSharp", {"position": v(3.75, 55.1) * mm});
            skArc(sketch, "E200.filletArc", {"start": v(2.98, 55.1) * mm, "mid": v(3.59, 55.3) * mm, "end": v(3.94, 55.85) * mm});
            skPoint(sketch, "E201.visualSharp", {"position": v(8.67, 56.7) * mm});
            skArc(sketch, "E201.filletArc", {"start": v(8.16, 56.7) * mm, "mid": v(8.61, 56.8) * mm, "end": v(8.97, 57.1) * mm});
            skPoint(sketch, "E202.visualSharp", {"position": v(18.2, 69.55) * mm});
            skArc(sketch, "E202.filletArc", {"start": v(17.71, 68.9) * mm, "mid": v(17.9, 69.54) * mm, "end": v(17.65, 70.16) * mm});
            skPoint(sketch, "E203.visualSharp", {"position": v(13.25, 75.05) * mm});
            skArc(sketch, "E203.filletArc", {"start": v(13.55, 74.72) * mm, "mid": v(13.21, 74.96) * mm, "end": v(12.8, 75.05) * mm});
            skPoint(sketch, "E204.visualSharp", {"position": v(9.75, 75.05) * mm});
            skArc(sketch, "E204.filletArc", {"start": v(10.44, 75.05) * mm, "mid": v(9.87, 74.87) * mm, "end": v(9.5, 74.4) * mm});
            skArc(sketch, "E205.MirrorCS", {"start": v(-13.55, 74.72) * mm, "mid": v(-13.21, 74.96) * mm, "end": v(-12.8, 75.05) * mm});
            skArc(sketch, "E206.MirrorCS", {"start": v(-2.98, 55.1) * mm, "mid": v(-3.59, 55.3) * mm, "end": v(-3.94, 55.85) * mm});
            skArc(sketch, "E207.MirrorCS", {"start": v(-17.71, 68.9) * mm, "mid": v(-17.9, 69.54) * mm, "end": v(-17.65, 70.16) * mm});
            skLineSegment(sketch, "E208.MirrorCS", {"start": v(-10.44, 75.05) * mm, "end": v(-12.8, 75.05) * mm});
            skArc(sketch, "E209.MirrorCS", {"start": v(-10.44, 75.05) * mm, "mid": v(-9.87, 74.87) * mm, "end": v(-9.5, 74.4) * mm});
            skArc(sketch, "E210.MirrorCS", {"start": v(-8.16, 56.7) * mm, "mid": v(-8.61, 56.8) * mm, "end": v(-8.97, 57.1) * mm});
            skLineSegment(sketch, "E211.MirrorCS", {"start": v(-3.94, 55.85) * mm, "end": v(-4.17, 56.7) * mm});
            skLineSegment(sketch, "E212.MirrorCS", {"start": v(-9, 73.1) * mm, "end": v(-9.5, 74.4) * mm});
            skLineSegment(sketch, "E213.MirrorCS", {"start": v(-4.17, 56.7) * mm, "end": v(-8.16, 56.7) * mm});
            skLineSegment(sketch, "E214.MirrorCS", {"start": v(-2.98, 55.1) * mm, "end": v(0, 55.1) * mm});
            skLineSegment(sketch, "E215.MirrorCS", {"start": v(-13.55, 74.72) * mm, "end": v(-17.65, 70.16) * mm});
            skPoint(sketch, "E216.MirrorP", {"position": v(-18.2, 69.55) * mm});
            skLineSegment(sketch, "E217.MirrorCS", {"start": v(0, 73.1) * mm, "end": v(-9, 73.1) * mm});
            skPoint(sketch, "E218.MirrorP", {"position": v(-3.75, 55.1) * mm});
            skPoint(sketch, "E219.MirrorP", {"position": v(-9.75, 75.05) * mm});
            skPoint(sketch, "E220.MirrorP", {"position": v(-13.25, 75.05) * mm});
            skPoint(sketch, "E221.MirrorP", {"position": v(-8.67, 56.7) * mm});
            skLineSegment(sketch, "E222.MirrorCS", {"start": v(-17.71, 68.9) * mm, "end": v(-8.97, 57.1) * mm});
            skPoint(sketch, "E223.1.0", {"position": v(-53.44, 20.84) * mm});
            skPoint(sketch, "E223.1.1", {"position": v(-60.12, 45.97) * mm});
            skPoint(sketch, "E223.1.2", {"position": v(-71.62, 26.05) * mm});
            skPoint(sketch, "E223.1.3", {"position": v(-49.6, 24.3) * mm});
            skLineSegment(sketch, "E223.1.4", {"start": v(-68.52, 19.1) * mm, "end": v(-53.94, 20.79) * mm});
            skPoint(sketch, "E223.1.5", {"position": v(-51.13, 50.54) * mm});
            skLineSegment(sketch, "E223.1.6", {"start": v(-63.3, 36.55) * mm, "end": v(-67.8, 28.76) * mm});
            skPoint(sketch, "E223.1.7", {"position": v(-69.87, 29.08) * mm});
            skPoint(sketch, "E223.1.8", {"position": v(-58.37, 49) * mm});
            skLineSegment(sketch, "E223.1.9", {"start": v(-50.8, 49.79) * mm, "end": v(-44.97, 36.32) * mm});
            skLineSegment(sketch, "E223.1.10", {"start": v(-71.48, 25.62) * mm, "end": v(-69.59, 19.8) * mm});
            skLineSegment(sketch, "E223.1.11", {"start": v(-57.93, 49.1) * mm, "end": v(-51.93, 50.37) * mm});
            skLineSegment(sketch, "E223.1.12", {"start": v(-63.3, 36.55) * mm, "end": v(-58.8, 44.34) * mm});
            skPoint(sketch, "E223.1.13", {"position": v(-45.84, 30.8) * mm});
            skPoint(sketch, "E223.1.14", {"position": v(-69.33, 19.01) * mm});
            skPoint(sketch, "E223.1.15", {"position": v(-44.77, 35.86) * mm});
            skLineSegment(sketch, "E223.1.16", {"start": v(-46.23, 30.13) * mm, "end": v(-47.72, 27.55) * mm});
            skLineSegment(sketch, "E223.1.17", {"start": v(-49.2, 24.97) * mm, "end": v(-47.72, 27.55) * mm});
            skLineSegment(sketch, "E223.1.18", {"start": v(-58.8, 44.34) * mm, "end": v(-59.69, 45.44) * mm});
            skArc(sketch, "E223.1.19", {"start": v(-70.21, 28.49) * mm, "mid": v(-69.78, 28.89) * mm, "end": v(-69.2, 28.97) * mm});
            skArc(sketch, "E223.1.20", {"start": v(-49.2, 24.97) * mm, "mid": v(-49.7, 24.55) * mm, "end": v(-50.34, 24.5) * mm});
            skArc(sketch, "E223.1.21", {"start": v(-45.02, 35.42) * mm, "mid": v(-44.89, 35.86) * mm, "end": v(-44.97, 36.32) * mm});
            skLineSegment(sketch, "E223.1.22", {"start": v(-46.4, 31.34) * mm, "end": v(-47.02, 31.96) * mm});
            skLineSegment(sketch, "E223.1.23", {"start": v(-51.19, 24.74) * mm, "end": v(-53.19, 21.28) * mm});
            skLineSegment(sketch, "E223.1.24", {"start": v(-70.21, 28.49) * mm, "end": v(-71.4, 26.43) * mm});
            skArc(sketch, "E223.1.25", {"start": v(-46.23, 30.13) * mm, "mid": v(-46.1, 30.76) * mm, "end": v(-46.4, 31.34) * mm});
            skArc(sketch, "E223.1.26", {"start": v(-68.52, 19.1) * mm, "mid": v(-69.17, 19.26) * mm, "end": v(-69.59, 19.8) * mm});
            skArc(sketch, "E223.1.27", {"start": v(-50.8, 49.79) * mm, "mid": v(-51.27, 50.28) * mm, "end": v(-51.93, 50.37) * mm});
            skArc(sketch, "E223.1.28", {"start": v(-71.48, 25.62) * mm, "mid": v(-71.53, 26.04) * mm, "end": v(-71.4, 26.43) * mm});
            skLineSegment(sketch, "E223.1.29", {"start": v(-47.02, 31.96) * mm, "end": v(-45.02, 35.42) * mm});
            skLineSegment(sketch, "E223.1.30", {"start": v(-59.78, 46.56) * mm, "end": v(-58.6, 48.62) * mm});
            skArc(sketch, "E223.1.31", {"start": v(-53.19, 21.28) * mm, "mid": v(-53.5, 20.94) * mm, "end": v(-53.94, 20.79) * mm});
            skLineSegment(sketch, "E223.1.32", {"start": v(-67.8, 28.76) * mm, "end": v(-69.2, 28.97) * mm});
            skLineSegment(sketch, "E223.1.33", {"start": v(-50.34, 24.5) * mm, "end": v(-51.19, 24.74) * mm});
            skArc(sketch, "E223.1.34", {"start": v(-59.78, 46.56) * mm, "mid": v(-59.9, 45.99) * mm, "end": v(-59.69, 45.44) * mm});
            skArc(sketch, "E223.1.35", {"start": v(-57.93, 49.1) * mm, "mid": v(-58.31, 48.93) * mm, "end": v(-58.6, 48.62) * mm});
            skPoint(sketch, "E223.2.0", {"position": v(-44.77, -35.86) * mm});
            skPoint(sketch, "E223.2.1", {"position": v(-69.87, -29.08) * mm});
            skPoint(sketch, "E223.2.2", {"position": v(-58.37, -49) * mm});
            skPoint(sketch, "E223.2.3", {"position": v(-45.84, -30.8) * mm});
            skLineSegment(sketch, "E223.2.4", {"start": v(-50.8, -49.79) * mm, "end": v(-44.97, -36.32) * mm});
            skPoint(sketch, "E223.2.5", {"position": v(-69.33, -19.01) * mm});
            skLineSegment(sketch, "E223.2.6", {"start": v(-63.3, -36.55) * mm, "end": v(-58.8, -44.34) * mm});
            skPoint(sketch, "E223.2.7", {"position": v(-60.12, -45.97) * mm});
            skPoint(sketch, "E223.2.8", {"position": v(-71.62, -26.05) * mm});
            skLineSegment(sketch, "E223.2.9", {"start": v(-68.52, -19.1) * mm, "end": v(-53.94, -20.79) * mm});
            skLineSegment(sketch, "E223.2.10", {"start": v(-57.93, -49.1) * mm, "end": v(-51.93, -50.37) * mm});
            skLineSegment(sketch, "E223.2.11", {"start": v(-71.48, -25.62) * mm, "end": v(-69.59, -19.8) * mm});
            skLineSegment(sketch, "E223.2.12", {"start": v(-63.3, -36.55) * mm, "end": v(-67.8, -28.76) * mm});
            skPoint(sketch, "E223.2.13", {"position": v(-49.6, -24.3) * mm});
            skPoint(sketch, "E223.2.14", {"position": v(-51.13, -50.54) * mm});
            skPoint(sketch, "E223.2.15", {"position": v(-53.44, -20.84) * mm});
            skLineSegment(sketch, "E223.2.16", {"start": v(-49.2, -24.97) * mm, "end": v(-47.72, -27.55) * mm});
            skLineSegment(sketch, "E223.2.17", {"start": v(-46.23, -30.13) * mm, "end": v(-47.72, -27.55) * mm});
            skLineSegment(sketch, "E223.2.18", {"start": v(-67.8, -28.76) * mm, "end": v(-69.2, -28.97) * mm});
            skArc(sketch, "E223.2.19", {"start": v(-59.78, -46.56) * mm, "mid": v(-59.9, -45.99) * mm, "end": v(-59.69, -45.44) * mm});
            skArc(sketch, "E223.2.20", {"start": v(-46.23, -30.13) * mm, "mid": v(-46.1, -30.76) * mm, "end": v(-46.4, -31.34) * mm});
            skArc(sketch, "E223.2.21", {"start": v(-53.19, -21.28) * mm, "mid": v(-53.5, -20.94) * mm, "end": v(-53.94, -20.79) * mm});
            skLineSegment(sketch, "E223.2.22", {"start": v(-50.34, -24.5) * mm, "end": v(-51.19, -24.74) * mm});
            skLineSegment(sketch, "E223.2.23", {"start": v(-47.02, -31.96) * mm, "end": v(-45.02, -35.42) * mm});
            skLineSegment(sketch, "E223.2.24", {"start": v(-59.78, -46.56) * mm, "end": v(-58.6, -48.62) * mm});
            skArc(sketch, "E223.2.25", {"start": v(-49.2, -24.97) * mm, "mid": v(-49.7, -24.55) * mm, "end": v(-50.34, -24.5) * mm});
            skArc(sketch, "E223.2.26", {"start": v(-50.8, -49.79) * mm, "mid": v(-51.27, -50.28) * mm, "end": v(-51.93, -50.37) * mm});
            skArc(sketch, "E223.2.27", {"start": v(-68.52, -19.1) * mm, "mid": v(-69.17, -19.26) * mm, "end": v(-69.59, -19.8) * mm});
            skArc(sketch, "E223.2.28", {"start": v(-57.93, -49.1) * mm, "mid": v(-58.31, -48.93) * mm, "end": v(-58.6, -48.62) * mm});
            skLineSegment(sketch, "E223.2.29", {"start": v(-51.19, -24.74) * mm, "end": v(-53.19, -21.28) * mm});
            skLineSegment(sketch, "E223.2.30", {"start": v(-70.21, -28.49) * mm, "end": v(-71.4, -26.43) * mm});
            skArc(sketch, "E223.2.31", {"start": v(-45.02, -35.42) * mm, "mid": v(-44.89, -35.86) * mm, "end": v(-44.97, -36.32) * mm});
            skLineSegment(sketch, "E223.2.32", {"start": v(-58.8, -44.34) * mm, "end": v(-59.69, -45.44) * mm});
            skLineSegment(sketch, "E223.2.33", {"start": v(-46.4, -31.34) * mm, "end": v(-47.02, -31.96) * mm});
            skArc(sketch, "E223.2.34", {"start": v(-70.21, -28.49) * mm, "mid": v(-69.78, -28.89) * mm, "end": v(-69.2, -28.97) * mm});
            skArc(sketch, "E223.2.35", {"start": v(-71.48, -25.62) * mm, "mid": v(-71.53, -26.04) * mm, "end": v(-71.4, -26.43) * mm});
            skPoint(sketch, "E223.3.0", {"position": v(8.67, -56.7) * mm});
            skPoint(sketch, "E223.3.1", {"position": v(-9.75, -75.05) * mm});
            skPoint(sketch, "E223.3.2", {"position": v(13.25, -75.05) * mm});
            skPoint(sketch, "E223.3.3", {"position": v(3.75, -55.1) * mm});
            skLineSegment(sketch, "E223.3.4", {"start": v(17.71, -68.9) * mm, "end": v(8.97, -57.1) * mm});
            skPoint(sketch, "E223.3.5", {"position": v(-18.2, -69.55) * mm});
            skLineSegment(sketch, "E223.3.6", {"start": v(0, -73.1) * mm, "end": v(9, -73.1) * mm});
            skPoint(sketch, "E223.3.7", {"position": v(9.75, -75.05) * mm});
            skPoint(sketch, "E223.3.8", {"position": v(-13.25, -75.05) * mm});
            skLineSegment(sketch, "E223.3.9", {"start": v(-17.71, -68.9) * mm, "end": v(-8.97, -57.1) * mm});
            skLineSegment(sketch, "E223.3.10", {"start": v(13.55, -74.72) * mm, "end": v(17.65, -70.16) * mm});
            skLineSegment(sketch, "E223.3.11", {"start": v(-13.55, -74.72) * mm, "end": v(-17.65, -70.16) * mm});
            skLineSegment(sketch, "E223.3.12", {"start": v(0, -73.1) * mm, "end": v(-9, -73.1) * mm});
            skPoint(sketch, "E223.3.13", {"position": v(-3.75, -55.1) * mm});
            skPoint(sketch, "E223.3.14", {"position": v(18.2, -69.55) * mm});
            skPoint(sketch, "E223.3.15", {"position": v(-8.67, -56.7) * mm});
            skLineSegment(sketch, "E223.3.16", {"start": v(-2.98, -55.1) * mm, "end": v(0, -55.1) * mm});
            skLineSegment(sketch, "E223.3.17", {"start": v(2.98, -55.1) * mm, "end": v(0, -55.1) * mm});
            skLineSegment(sketch, "E223.3.18", {"start": v(-9, -73.1) * mm, "end": v(-9.5, -74.4) * mm});
            skArc(sketch, "E223.3.19", {"start": v(10.44, -75.05) * mm, "mid": v(9.87, -74.87) * mm, "end": v(9.5, -74.4) * mm});
            skArc(sketch, "E223.3.20", {"start": v(2.98, -55.1) * mm, "mid": v(3.59, -55.3) * mm, "end": v(3.94, -55.85) * mm});
            skArc(sketch, "E223.3.21", {"start": v(-8.16, -56.7) * mm, "mid": v(-8.61, -56.8) * mm, "end": v(-8.97, -57.1) * mm});
            skLineSegment(sketch, "E223.3.22", {"start": v(-3.94, -55.85) * mm, "end": v(-4.17, -56.7) * mm});
            skLineSegment(sketch, "E223.3.23", {"start": v(4.17, -56.7) * mm, "end": v(8.16, -56.7) * mm});
            skLineSegment(sketch, "E223.3.24", {"start": v(10.44, -75.05) * mm, "end": v(12.8, -75.05) * mm});
            skArc(sketch, "E223.3.25", {"start": v(-2.98, -55.1) * mm, "mid": v(-3.59, -55.3) * mm, "end": v(-3.94, -55.85) * mm});
            skArc(sketch, "E223.3.26", {"start": v(17.71, -68.9) * mm, "mid": v(17.9, -69.54) * mm, "end": v(17.65, -70.16) * mm});
            skArc(sketch, "E223.3.27", {"start": v(-17.71, -68.9) * mm, "mid": v(-17.9, -69.54) * mm, "end": v(-17.65, -70.16) * mm});
            skArc(sketch, "E223.3.28", {"start": v(13.55, -74.72) * mm, "mid": v(13.21, -74.96) * mm, "end": v(12.8, -75.05) * mm});
            skLineSegment(sketch, "E223.3.29", {"start": v(-4.17, -56.7) * mm, "end": v(-8.16, -56.7) * mm});
            skLineSegment(sketch, "E223.3.30", {"start": v(-10.44, -75.05) * mm, "end": v(-12.8, -75.05) * mm});
            skArc(sketch, "E223.3.31", {"start": v(8.16, -56.7) * mm, "mid": v(8.61, -56.8) * mm, "end": v(8.97, -57.1) * mm});
            skLineSegment(sketch, "E223.3.32", {"start": v(9, -73.1) * mm, "end": v(9.5, -74.4) * mm});
            skLineSegment(sketch, "E223.3.33", {"start": v(3.94, -55.85) * mm, "end": v(4.17, -56.7) * mm});
            skArc(sketch, "E223.3.34", {"start": v(-10.44, -75.05) * mm, "mid": v(-9.87, -74.87) * mm, "end": v(-9.5, -74.4) * mm});
            skArc(sketch, "E223.3.35", {"start": v(-13.55, -74.72) * mm, "mid": v(-13.21, -74.96) * mm, "end": v(-12.8, -75.05) * mm});
            skPoint(sketch, "E223.4.0", {"position": v(53.44, -20.84) * mm});
            skPoint(sketch, "E223.4.1", {"position": v(60.12, -45.97) * mm});
            skPoint(sketch, "E223.4.2", {"position": v(71.62, -26.05) * mm});
            skPoint(sketch, "E223.4.3", {"position": v(49.6, -24.3) * mm});
            skLineSegment(sketch, "E223.4.4", {"start": v(68.52, -19.1) * mm, "end": v(53.94, -20.79) * mm});
            skPoint(sketch, "E223.4.5", {"position": v(51.13, -50.54) * mm});
            skLineSegment(sketch, "E223.4.6", {"start": v(63.3, -36.55) * mm, "end": v(67.8, -28.76) * mm});
            skPoint(sketch, "E223.4.7", {"position": v(69.87, -29.08) * mm});
            skPoint(sketch, "E223.4.8", {"position": v(58.37, -49) * mm});
            skLineSegment(sketch, "E223.4.9", {"start": v(50.8, -49.79) * mm, "end": v(44.97, -36.32) * mm});
            skLineSegment(sketch, "E223.4.10", {"start": v(71.48, -25.62) * mm, "end": v(69.59, -19.8) * mm});
            skLineSegment(sketch, "E223.4.11", {"start": v(57.93, -49.1) * mm, "end": v(51.93, -50.37) * mm});
            skLineSegment(sketch, "E223.4.12", {"start": v(63.3, -36.55) * mm, "end": v(58.8, -44.34) * mm});
            skPoint(sketch, "E223.4.13", {"position": v(45.84, -30.8) * mm});
            skPoint(sketch, "E223.4.14", {"position": v(69.33, -19.01) * mm});
            skPoint(sketch, "E223.4.15", {"position": v(44.77, -35.86) * mm});
            skLineSegment(sketch, "E223.4.16", {"start": v(46.23, -30.13) * mm, "end": v(47.72, -27.55) * mm});
            skLineSegment(sketch, "E223.4.17", {"start": v(49.2, -24.97) * mm, "end": v(47.72, -27.55) * mm});
            skLineSegment(sketch, "E223.4.18", {"start": v(58.8, -44.34) * mm, "end": v(59.69, -45.44) * mm});
            skArc(sketch, "E223.4.19", {"start": v(70.21, -28.49) * mm, "mid": v(69.78, -28.89) * mm, "end": v(69.2, -28.97) * mm});
            skArc(sketch, "E223.4.20", {"start": v(49.2, -24.97) * mm, "mid": v(49.7, -24.55) * mm, "end": v(50.34, -24.5) * mm});
            skArc(sketch, "E223.4.21", {"start": v(45.02, -35.42) * mm, "mid": v(44.89, -35.86) * mm, "end": v(44.97, -36.32) * mm});
            skLineSegment(sketch, "E223.4.22", {"start": v(46.4, -31.34) * mm, "end": v(47.02, -31.96) * mm});
            skLineSegment(sketch, "E223.4.23", {"start": v(51.19, -24.74) * mm, "end": v(53.19, -21.28) * mm});
            skLineSegment(sketch, "E223.4.24", {"start": v(70.21, -28.49) * mm, "end": v(71.4, -26.43) * mm});
            skArc(sketch, "E223.4.25", {"start": v(46.23, -30.13) * mm, "mid": v(46.1, -30.76) * mm, "end": v(46.4, -31.34) * mm});
            skArc(sketch, "E223.4.26", {"start": v(68.52, -19.1) * mm, "mid": v(69.17, -19.26) * mm, "end": v(69.59, -19.8) * mm});
            skArc(sketch, "E223.4.27", {"start": v(50.8, -49.79) * mm, "mid": v(51.27, -50.28) * mm, "end": v(51.93, -50.37) * mm});
            skArc(sketch, "E223.4.28", {"start": v(71.48, -25.62) * mm, "mid": v(71.53, -26.04) * mm, "end": v(71.4, -26.43) * mm});
            skLineSegment(sketch, "E223.4.29", {"start": v(47.02, -31.96) * mm, "end": v(45.02, -35.42) * mm});
            skLineSegment(sketch, "E223.4.30", {"start": v(59.78, -46.56) * mm, "end": v(58.6, -48.62) * mm});
            skArc(sketch, "E223.4.31", {"start": v(53.19, -21.28) * mm, "mid": v(53.5, -20.94) * mm, "end": v(53.94, -20.79) * mm});
            skLineSegment(sketch, "E223.4.32", {"start": v(67.8, -28.76) * mm, "end": v(69.2, -28.97) * mm});
            skLineSegment(sketch, "E223.4.33", {"start": v(50.34, -24.5) * mm, "end": v(51.19, -24.74) * mm});
            skArc(sketch, "E223.4.34", {"start": v(59.78, -46.56) * mm, "mid": v(59.9, -45.99) * mm, "end": v(59.69, -45.44) * mm});
            skArc(sketch, "E223.4.35", {"start": v(57.93, -49.1) * mm, "mid": v(58.31, -48.93) * mm, "end": v(58.6, -48.62) * mm});
            skPoint(sketch, "E223.5.0", {"position": v(44.77, 35.86) * mm});
            skPoint(sketch, "E223.5.1", {"position": v(69.87, 29.08) * mm});
            skPoint(sketch, "E223.5.2", {"position": v(58.37, 49) * mm});
            skPoint(sketch, "E223.5.3", {"position": v(45.84, 30.8) * mm});
            skLineSegment(sketch, "E223.5.4", {"start": v(50.8, 49.79) * mm, "end": v(44.97, 36.32) * mm});
            skPoint(sketch, "E223.5.5", {"position": v(69.33, 19.01) * mm});
            skLineSegment(sketch, "E223.5.6", {"start": v(63.3, 36.55) * mm, "end": v(58.8, 44.34) * mm});
            skPoint(sketch, "E223.5.7", {"position": v(60.12, 45.97) * mm});
            skPoint(sketch, "E223.5.8", {"position": v(71.62, 26.05) * mm});
            skLineSegment(sketch, "E223.5.9", {"start": v(68.52, 19.1) * mm, "end": v(53.94, 20.79) * mm});
            skLineSegment(sketch, "E223.5.10", {"start": v(57.93, 49.1) * mm, "end": v(51.93, 50.37) * mm});
            skLineSegment(sketch, "E223.5.11", {"start": v(71.48, 25.62) * mm, "end": v(69.59, 19.8) * mm});
            skLineSegment(sketch, "E223.5.12", {"start": v(63.3, 36.55) * mm, "end": v(67.8, 28.76) * mm});
            skPoint(sketch, "E223.5.13", {"position": v(49.6, 24.3) * mm});
            skPoint(sketch, "E223.5.14", {"position": v(51.13, 50.54) * mm});
            skPoint(sketch, "E223.5.15", {"position": v(53.44, 20.84) * mm});
            skLineSegment(sketch, "E223.5.16", {"start": v(49.2, 24.97) * mm, "end": v(47.72, 27.55) * mm});
            skLineSegment(sketch, "E223.5.17", {"start": v(46.23, 30.13) * mm, "end": v(47.72, 27.55) * mm});
            skLineSegment(sketch, "E223.5.18", {"start": v(67.8, 28.76) * mm, "end": v(69.2, 28.97) * mm});
            skArc(sketch, "E223.5.19", {"start": v(59.78, 46.56) * mm, "mid": v(59.9, 45.99) * mm, "end": v(59.69, 45.44) * mm});
            skArc(sketch, "E223.5.20", {"start": v(46.23, 30.13) * mm, "mid": v(46.1, 30.76) * mm, "end": v(46.4, 31.34) * mm});
            skArc(sketch, "E223.5.21", {"start": v(53.19, 21.28) * mm, "mid": v(53.5, 20.94) * mm, "end": v(53.94, 20.79) * mm});
            skLineSegment(sketch, "E223.5.22", {"start": v(50.34, 24.5) * mm, "end": v(51.19, 24.74) * mm});
            skLineSegment(sketch, "E223.5.23", {"start": v(47.02, 31.96) * mm, "end": v(45.02, 35.42) * mm});
            skLineSegment(sketch, "E223.5.24", {"start": v(59.78, 46.56) * mm, "end": v(58.6, 48.62) * mm});
            skArc(sketch, "E223.5.25", {"start": v(49.2, 24.97) * mm, "mid": v(49.7, 24.55) * mm, "end": v(50.34, 24.5) * mm});
            skArc(sketch, "E223.5.26", {"start": v(50.8, 49.79) * mm, "mid": v(51.27, 50.28) * mm, "end": v(51.93, 50.37) * mm});
            skArc(sketch, "E223.5.27", {"start": v(68.52, 19.1) * mm, "mid": v(69.17, 19.26) * mm, "end": v(69.59, 19.8) * mm});
            skArc(sketch, "E223.5.28", {"start": v(57.93, 49.1) * mm, "mid": v(58.31, 48.93) * mm, "end": v(58.6, 48.62) * mm});
            skLineSegment(sketch, "E223.5.29", {"start": v(51.19, 24.74) * mm, "end": v(53.19, 21.28) * mm});
            skLineSegment(sketch, "E223.5.30", {"start": v(70.21, 28.49) * mm, "end": v(71.4, 26.43) * mm});
            skArc(sketch, "E223.5.31", {"start": v(45.02, 35.42) * mm, "mid": v(44.89, 35.86) * mm, "end": v(44.97, 36.32) * mm});
            skLineSegment(sketch, "E223.5.32", {"start": v(58.8, 44.34) * mm, "end": v(59.69, 45.44) * mm});
            skLineSegment(sketch, "E223.5.33", {"start": v(46.4, 31.34) * mm, "end": v(47.02, 31.96) * mm});
            skArc(sketch, "E223.5.34", {"start": v(70.21, 28.49) * mm, "mid": v(69.78, 28.89) * mm, "end": v(69.2, 28.97) * mm});
            skArc(sketch, "E223.5.35", {"start": v(71.48, 25.62) * mm, "mid": v(71.53, 26.04) * mm, "end": v(71.4, 26.43) * mm});
            skSolve(sketch);
        }
        {
            var Q0;
            Q0 = qSketchRegion(id + "F16", true);
            extrude(context, id + "F17", {"entities" : qUnion([Q0]), "operationType" : NewBodyOperationType.REMOVE, "oppositeDirection" : true, "depth" : 25 * mm, "offsetDistance" : 25 * mm});
        }
        {
            var Q0;
            {var subQ0=sQuery(id+"F0.wireOp",EDGE,"E0.5");var subQ1=sQuery(id+"F0.wireOp",EDGE,"E0.4");var subQ2=sQuery(id+"F0.wireOp",EDGE,"E0.3");var subQ3=sQuery(id+"F0.wireOp",EDGE,"E0.2");var subQ4=sQuery(id+"F0.wireOp",EDGE,"E0.1");var subQ5=sQuery(id+"F0.wireOp",EDGE,"E0.0");Q0=makeQuery(id+"F15.boolean.opBoolean","SPLIT",FACE,{"disambiguationData":[TD([makeQuery(id+"F1.opExtrude","SWEPT_FACE",FACE,{"disambiguationData":[OSD([subQ5])]})])],"derivedFrom":makeQuery(id+"F1.opExtrude","CAP_FACE",FACE,{"disambiguationData":[OSD([subQ5,subQ4,subQ3,subQ2,subQ1,subQ0])],"isStart":false})});}
            var sketch = newSketch(context, id + "F18", { "sketchPlane" : qUnion([Q0])});
            skLineSegment(sketch, "E224", {"start": v(0, 0) * mm, "end": v(-66.5, 0) * mm, "construction": true});
            skLineSegment(sketch, "E225", {"start": v(-66.5, 0) * mm, "end": v(-66.5, 1.9) * mm});
            skLineSegment(sketch, "E226", {"start": v(-65.5, 2.9) * mm, "end": v(-62, 2.9) * mm});
            skLineSegment(sketch, "E227", {"start": v(-62, 2.9) * mm, "end": v(-60.64, 4.22) * mm});
            skLineSegment(sketch, "E228", {"start": v(-59.94, 4.5) * mm, "end": v(-54.85, 4.5) * mm});
            skLineSegment(sketch, "E229", {"start": v(-54.85, 4.5) * mm, "end": v(-54.85, 0) * mm, "construction": true});
            skLineSegment(sketch, "E230.MirrorCS", {"start": v(-47.7, 2.9) * mm, "end": v(-49.06, 4.22) * mm});
            skLineSegment(sketch, "E231.MirrorCS", {"start": v(-49.76, 4.5) * mm, "end": v(-54.85, 4.5) * mm});
            skLineSegment(sketch, "E232.MirrorCS", {"start": v(-44.2, 2.9) * mm, "end": v(-47.7, 2.9) * mm});
            skLineSegment(sketch, "E233.MirrorCS", {"start": v(-43.2, 0) * mm, "end": v(-43.2, 1.9) * mm});
            skLineSegment(sketch, "E234.MirrorCS", {"start": v(-47.7, -2.9) * mm, "end": v(-49.06, -4.22) * mm});
            skLineSegment(sketch, "E235.MirrorCS", {"start": v(-62, -2.9) * mm, "end": v(-60.64, -4.22) * mm});
            skLineSegment(sketch, "E236.MirrorCS", {"start": v(-43.2, 0) * mm, "end": v(-43.2, -1.9) * mm});
            skLineSegment(sketch, "E237.MirrorCS", {"start": v(-65.5, -2.9) * mm, "end": v(-62, -2.9) * mm});
            skLineSegment(sketch, "E238.MirrorCS", {"start": v(-49.76, -4.5) * mm, "end": v(-54.85, -4.5) * mm});
            skLineSegment(sketch, "E239.MirrorCS", {"start": v(-54.85, -4.5) * mm, "end": v(-54.85, 0) * mm, "construction": true});
            skLineSegment(sketch, "E240.MirrorCS", {"start": v(-44.2, -2.9) * mm, "end": v(-47.7, -2.9) * mm});
            skLineSegment(sketch, "E241.MirrorCS", {"start": v(-66.5, 0) * mm, "end": v(-66.5, -1.9) * mm});
            skLineSegment(sketch, "E242.MirrorCS", {"start": v(-59.94, -4.5) * mm, "end": v(-54.85, -4.5) * mm});
            skLineSegment(sketch, "E243.MirrorCS", {"start": v(62, -2.9) * mm, "end": v(60.64, -4.22) * mm});
            skLineSegment(sketch, "E244.MirrorCS", {"start": v(62, 2.9) * mm, "end": v(60.64, 4.22) * mm});
            skLineSegment(sketch, "E245.MirrorCS", {"start": v(47.7, 2.9) * mm, "end": v(49.06, 4.22) * mm});
            skLineSegment(sketch, "E246.MirrorCS", {"start": v(59.94, -4.5) * mm, "end": v(54.85, -4.5) * mm});
            skLineSegment(sketch, "E247.MirrorCS", {"start": v(54.85, 4.5) * mm, "end": v(54.85, 0) * mm, "construction": true});
            skLineSegment(sketch, "E248.MirrorCS", {"start": v(49.76, 4.5) * mm, "end": v(54.85, 4.5) * mm});
            skLineSegment(sketch, "E249.MirrorCS", {"start": v(66.5, 0) * mm, "end": v(66.5, -1.9) * mm});
            skLineSegment(sketch, "E250.MirrorCS", {"start": v(43.2, 0) * mm, "end": v(43.2, -1.9) * mm});
            skLineSegment(sketch, "E251.MirrorCS", {"start": v(49.76, -4.5) * mm, "end": v(54.85, -4.5) * mm});
            skLineSegment(sketch, "E252.MirrorCS", {"start": v(65.5, -2.9) * mm, "end": v(62, -2.9) * mm});
            skLineSegment(sketch, "E253.MirrorCS", {"start": v(59.94, 4.5) * mm, "end": v(54.85, 4.5) * mm});
            skLineSegment(sketch, "E254.MirrorCS", {"start": v(44.2, -2.9) * mm, "end": v(47.7, -2.9) * mm});
            skLineSegment(sketch, "E255.MirrorCS", {"start": v(66.5, 0) * mm, "end": v(66.5, 1.9) * mm});
            skLineSegment(sketch, "E256.MirrorCS", {"start": v(54.85, -4.5) * mm, "end": v(54.85, 0) * mm, "construction": true});
            skLineSegment(sketch, "E257.MirrorCS", {"start": v(43.2, 0) * mm, "end": v(43.2, 1.9) * mm});
            skLineSegment(sketch, "E258.MirrorCS", {"start": v(65.5, 2.9) * mm, "end": v(62, 2.9) * mm});
            skLineSegment(sketch, "E259.MirrorCS", {"start": v(47.7, -2.9) * mm, "end": v(49.06, -4.22) * mm});
            skLineSegment(sketch, "E260.MirrorCS", {"start": v(44.2, 2.9) * mm, "end": v(47.7, 2.9) * mm});
            skPoint(sketch, "E261.visualSharp", {"position": v(-66.5, 2.9) * mm});
            skArc(sketch, "E261.filletArc", {"start": v(-65.5, 2.9) * mm, "mid": v(-66.2, 2.6) * mm, "end": v(-66.5, 1.9) * mm});
            skPoint(sketch, "E262.visualSharp", {"position": v(-66.5, -2.9) * mm});
            skArc(sketch, "E262.filletArc", {"start": v(-66.5, -1.9) * mm, "mid": v(-66.2, -2.6) * mm, "end": v(-65.5, -2.9) * mm});
            skPoint(sketch, "E263.visualSharp", {"position": v(-60.35, 4.5) * mm});
            skArc(sketch, "E263.filletArc", {"start": v(-59.94, 4.5) * mm, "mid": v(-60.32, 4.43) * mm, "end": v(-60.64, 4.22) * mm});
            skPoint(sketch, "E264.visualSharp", {"position": v(-60.35, -4.5) * mm});
            skArc(sketch, "E264.filletArc", {"start": v(-60.64, -4.22) * mm, "mid": v(-60.32, -4.43) * mm, "end": v(-59.94, -4.5) * mm});
            skPoint(sketch, "E265.visualSharp", {"position": v(-49.35, -4.5) * mm});
            skArc(sketch, "E265.filletArc", {"start": v(-49.76, -4.5) * mm, "mid": v(-49.38, -4.43) * mm, "end": v(-49.06, -4.22) * mm});
            skPoint(sketch, "E266.visualSharp", {"position": v(-49.35, 4.5) * mm});
            skArc(sketch, "E266.filletArc", {"start": v(-49.06, 4.22) * mm, "mid": v(-49.38, 4.43) * mm, "end": v(-49.76, 4.5) * mm});
            skPoint(sketch, "E267.visualSharp", {"position": v(-43.2, 2.9) * mm});
            skArc(sketch, "E267.filletArc", {"start": v(-43.2, 1.9) * mm, "mid": v(-43.5, 2.6) * mm, "end": v(-44.2, 2.9) * mm});
            skPoint(sketch, "E268.visualSharp", {"position": v(-43.2, -2.9) * mm});
            skArc(sketch, "E268.filletArc", {"start": v(-44.2, -2.9) * mm, "mid": v(-43.5, -2.6) * mm, "end": v(-43.2, -1.9) * mm});
            skPoint(sketch, "E269.visualSharp", {"position": v(43.2, 2.9) * mm});
            skArc(sketch, "E269.filletArc", {"start": v(44.2, 2.9) * mm, "mid": v(43.5, 2.6) * mm, "end": v(43.2, 1.9) * mm});
            skPoint(sketch, "E270.visualSharp", {"position": v(43.2, -2.9) * mm});
            skArc(sketch, "E270.filletArc", {"start": v(43.2, -1.9) * mm, "mid": v(43.5, -2.6) * mm, "end": v(44.2, -2.9) * mm});
            skPoint(sketch, "E271.visualSharp", {"position": v(49.35, 4.5) * mm});
            skArc(sketch, "E271.filletArc", {"start": v(49.76, 4.5) * mm, "mid": v(49.38, 4.43) * mm, "end": v(49.06, 4.22) * mm});
            skPoint(sketch, "E272.visualSharp", {"position": v(60.35, 4.5) * mm});
            skArc(sketch, "E272.filletArc", {"start": v(60.64, 4.22) * mm, "mid": v(60.32, 4.43) * mm, "end": v(59.94, 4.5) * mm});
            skPoint(sketch, "E273.visualSharp", {"position": v(66.5, 2.9) * mm});
            skArc(sketch, "E273.filletArc", {"start": v(66.5, 1.9) * mm, "mid": v(66.2, 2.6) * mm, "end": v(65.5, 2.9) * mm});
            skPoint(sketch, "E274.visualSharp", {"position": v(66.5, -2.9) * mm});
            skArc(sketch, "E274.filletArc", {"start": v(65.5, -2.9) * mm, "mid": v(66.2, -2.6) * mm, "end": v(66.5, -1.9) * mm});
            skPoint(sketch, "E275.visualSharp", {"position": v(60.35, -4.5) * mm});
            skArc(sketch, "E275.filletArc", {"start": v(59.94, -4.5) * mm, "mid": v(60.32, -4.43) * mm, "end": v(60.64, -4.22) * mm});
            skPoint(sketch, "E276.visualSharp", {"position": v(49.35, -4.5) * mm});
            skArc(sketch, "E276.filletArc", {"start": v(49.06, -4.22) * mm, "mid": v(49.38, -4.43) * mm, "end": v(49.76, -4.5) * mm});
            skSolve(sketch);
        }
        {
            var Q0;
            Q0 = qSketchRegion(id + "F18", true);
            extrude(context, id + "F19", {"entities" : qUnion([Q0]), "operationType" : NewBodyOperationType.REMOVE, "oppositeDirection" : true, "depth" : 25 * mm, "offsetDistance" : 25 * mm});
        }
    });
